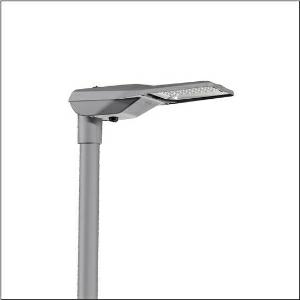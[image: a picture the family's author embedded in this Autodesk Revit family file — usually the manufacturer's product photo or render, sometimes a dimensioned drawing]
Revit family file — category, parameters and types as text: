
# Revit family: streetlight_sl_21_mini___st0_8a_5xe2c23t08hb_e0eb
name_source: partatom
category: Lighting Fixtures
units: mm (PartAtom-declared; Revit-internal decimal feet)

## family parameters
Cut with Voids When Loaded = No
Host = Face
Light Source = No
Part Type = Normal
Room Calculation Point = No
Round Connector Dimension = Use Diameter
Shared = No

## types (1)
- --- (1 x LED, 7490 lm, 66 W, 2200K)
    Apparent Load = 66 VA
    CIE Flux Codes = 38 75 97 100 100
    Color Rendering = 70
    Color Temperature = 2200K
    Default Elevation = 1800 mm
    Description = Streetlight SL 21 mini, mast luminaire, primary light control with lens, of PMMA, primary optical cover: cover, of toughened safety glass, transparent, light distribution: ST0.8a, light emission: direct distribution, primary light characteristic: asymmetric, installation type: side-entry, post-top, LED, High Power LED, rated luminous flux: 7.490lm, luminous efficacy: 114lm/W, light colour: 722, colour temperature: 2200K, control gear: D4i, control: overheat protection, constant luminous flux control, time-dependent luminous flux control, flexible luminous flux parameterisation, pre-setting: logarithmic dimming characteristic, mains connection: 220..240V, AC, 50/60Hz, start of lifetime: 66W, end of service life: 69W, reduction: 30W, luminaire housing, of diecast aluminium, powder-coated, SITECO metallic grey (DB 702S), corrosivity category C5 high according to DIN EN ISO 12944, please order mast flange separately, inclination adjustable: 0°, 5°, 10°, 15°, sealing non-destructively replaceable, multi-level sealing system, length: 628mm, width: 235mm, height: 110mm, mast flange for spigot size: 42mm (side-entry): 5XC10008XM4, 60/48mm (side-entry/post-top): 5XC10108XM2, 76/60mm (side-entry/post-top): 5XC10108XM1, mounting height: 4..8m, Smart Interface below and above, protection rating (complete): IP66, insulation class (complete): insulation class II (safety insulation), certification: CE, ENEC, ENEC+, VDE, impact resistance: IK10, permissible operating ambient temperature for outdoor applications: -40..+50°C, standard-compliant lighting for roads and squares, packaging unit: 1 piece

Light Distribution: ST0.8a
    Height = 110 mm
    Lamp = 1 x LED
    Lamp Light Flux = 7490 lm
    Lamp Power = 66 W
    Lamp count = 1
    Length = 625 mm
    Luminous efficacy = 113 lm/W
    Manufacturer = Siteco
    ModVariant = No
    Model = 5XE2C23T08HB
    Number of Poles = 1
    OnlyDefault = Yes
    Power Factor = 1
    Product Name = Streetlight SL 21 mini | ST0.8a
    Product group = mast luminaire | pylon top
    ProductGroupID = 6100
    Protection Class = Protection class II
    Protection Degree = IP 66
    RLX_Detail_Level = 1
    RLX_Emergency_Light_Flux = 0 lm
    RLX_Emergency_Type = 0
    RLX_Emergency_Type_DB = No
    RlxData = <blob elided: 26409 chars, md5=102290d0>
    Socket = socket
    Standby Power = 0 W
    System Light Flux = 7490 lm
    System Power = 66 W
    Type Comments = factory setting: luminous flux: 100 % | dim-lin: 254 | 670 mA
    Type Image = l_1003514.jpg
    URL = http://relux.com
    VarID = @adj_182807
    Voltage = 0 V
    Weight = 0.00 kg
    Width = 234 mm

## geometry (parser evidence)
native form markers: Blend x4, Sweep x12
no freeform markers — native parametric forms only
